# Revit family: 55-9504-Z5-M2
name_source: partatom
category: Luminarias
revit_build: Autodesk Revit 2017 (Build: 20160225_1515(x64)
units: mm (PartAtom-declared; Revit-internal decimal feet)

## family parameters
Compartido = Sí
Corte con vacíos al cargar = No
Cota de conector redondo = Diámetro de uso
Número OmniClass = 23.80.70.00
Origen de luz = No
Punto de cálculo de habitación = No
Se basa en plano de trabajo = No
Siempre vertical = Sí
Tipo de pieza = Normal
Título OmniClass = Lighting

## types (1)
- 55-9504-Z5-M2
    Acabado = Gris urbano, Transparente, Mate
    CRI = 0
    Catálogo = Outdoor
    CodigoGubimclass = 50.60.50.20
    CodigoOmniclass = 21-04 50 40
    CodigoUniclass2015 = EF_70_80
    CodigoUniformat2010 = D5040
    DescripcionGubimclass = Iluminación interior
    DescripcionOmniclass = Lighting
    DescripcionUniclass2015 = Lighting
    DescripcionUniformat2010 = Lighting
    EAN13 = 8435111082232
    Eficiencia energética = NO BULB
    Etiqueta V/f = 100-240V/50-60Hz
    Fabricante = LEDS C4
    Familia = Newton E27
    FechaVersion = Julio 2020
    Ficha = http://files.leds-c4.com
    IK = IK08
    IMC = http://files.leds-c4.com
    IP = IP65
    IfcExportAs = IfcLightFixture
    IfcExportType = NOTDEFINED
    Imagen web = http://files.leds-c4.com
    Lumenes reales (lm) = 0
    Material = Aluminio, Policarbonato, Cristal
    Peso neto (KG) = 3.42
    Pluma comercial = http://files.leds-c4.com
    Producto descatalogado = Catalogado ES
    Referencia = 55-9504-Z5-M2
    Tender text (Castellano) = LEDS C4
Newton E27
55-9504-Z5-M2V1

Baliza de uso exterior para iluminar ambos lados. 
Material estructura: Aluminio. Acabado estructura: Gris urbano. Material difusor: Policarbonato, Cristal. Acabado difusor: Transparente, Mate. Protección contra los rayos ultravioleta. Garantía: 5 Años.

Peso neto del producto (Kg): 3.420
Anchura o diámetro del producto (mm): 160
Altura del producto (mm): 800

Clase 1. IP: IP65. IK: IK08. E27. Longitud máxima de la bombilla que admite la luminaria: 155.000. Diámetro máximo de la bombilla que admite la luminaria: 55.000. Nº de portalámparas o Leds: 1. Potencia máxima de la fuente de luz: 23W. Equipo incluido: No. Potencia total: 23.
    Tender text (English) = LEDS C4
Newton E27
55-9504-Z5-M2V1

Bollard for outdoor use. 

For lighting both sides. Structure material: Aluminium. Structure finish: Urban grey. Diffuser material: Polycarbonate, Glass. Diffuser finish: Transparent, Matt. UV protection. Warranty: 5 Years.

Product net weight (Kg): 3.420
Product width or diameter (mm): 160
Product height (mm): 800

Class 1. IP: IP65. IK: IK08. E27. Maximum length of luminaire bulb: 155.000. Maximum diameter of luminaire bulb: 55.000. No. of lampholders or LEDs: 1. Maximum power of light source: 23W. Gear included: No. Total power: 23.
    Tipo = Baliza
    Vatios (W) = 23
    Versión = v1
